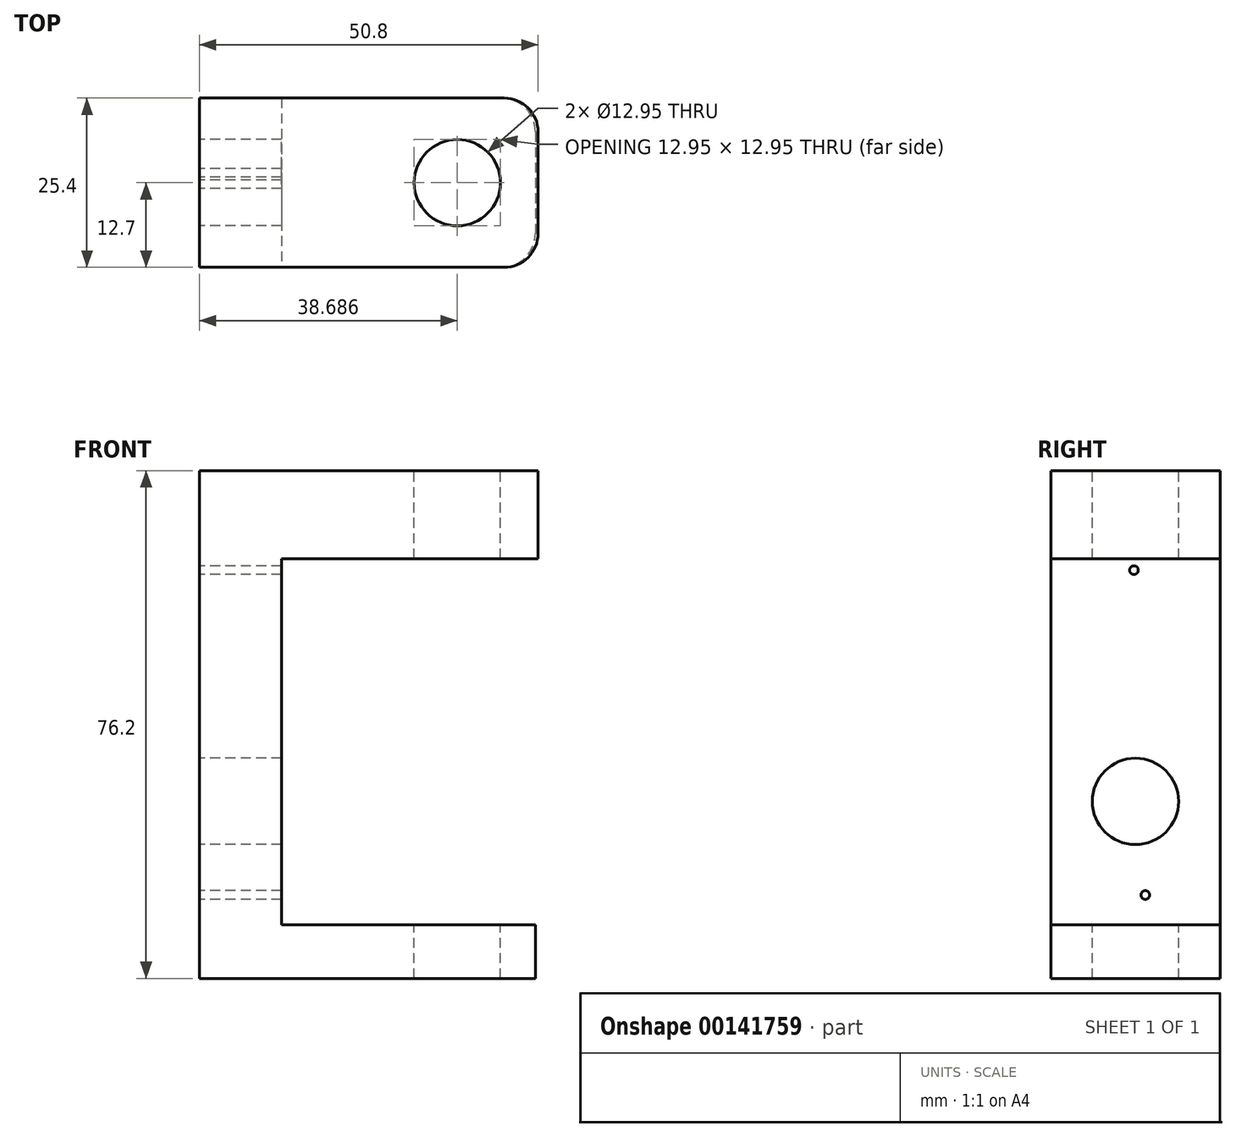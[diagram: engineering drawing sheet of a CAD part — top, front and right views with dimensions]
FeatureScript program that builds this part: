
annotation { "Feature Type Name" : "Feature", "Feature Type Description" : "" }
export const myFeature = defineFeature(function(context is Context, id is Id, definition is map)
    precondition{}
    {
        {
            var Q0;
            Q0=qCreatedBy(makeId("Top.planeOp"),FACE);
            var sketch = newSketch(context, id + "F0", { "sketchPlane" : qUnion([Q0])});
            skLineSegment(sketch, "E0.bottom", {"start": v(0, 0) * mm, "end": v(-50.8, 0) * mm});
            skLineSegment(sketch, "E0.top", {"start": v(0, 25.4) * mm, "end": v(-50.8, 25.4) * mm});
            skLineSegment(sketch, "E0.left", {"start": v(0, 0) * mm, "end": v(0, 25.4) * mm});
            skLineSegment(sketch, "E0.right", {"start": v(-50.8, 0) * mm, "end": v(-50.8, 25.4) * mm});
            skSolve(sketch);
        }
        {
            var Q0;
            Q0=makeQuery(id+"F0.imprint","IMPRINT",FACE,{"disambiguationData":[TD([[makeQuery(id+"F0.imprint","IMPRINT",EDGE,{"derivedFrom":sQuery(id+"F0.wireOp",EDGE,"E0.bottom")}),-1.0]])]});
            extrude(context, id + "F1", {"entities" : qUnion([Q0]), "depth" : 76.2 * mm});
        }
        {
            var Q0;
            Q0=makeQuery(id+"F1.opExtrude","SWEPT_FACE",FACE,{"disambiguationData":[OSD([sQuery(id+"F0.wireOp",EDGE,"E0.bottom")])]});
            var sketch = newSketch(context, id + "F2", { "sketchPlane" : qUnion([Q0])});
            skLineSegment(sketch, "E1.bottom", {"start": v(-38.5, 0) * mm, "end": v(0, 0) * mm});
            skLineSegment(sketch, "E1.top", {"start": v(-38.5, 63) * mm, "end": v(0, 63) * mm});
            skLineSegment(sketch, "E1.left", {"start": v(-38.5, 0) * mm, "end": v(-38.5, 63) * mm});
            skLineSegment(sketch, "E1.right", {"start": v(0, 0) * mm, "end": v(0, 63) * mm});
            skSolve(sketch);
        }
        {
            var Q0;
            Q0=makeQuery(id+"F2.imprint","IMPRINT",FACE,{"disambiguationData":[TD([[makeQuery(id+"F2.imprint","IMPRINT",EDGE,{"derivedFrom":sQuery(id+"F2.wireOp",EDGE,"E1.bottom")}),-1.0]])]});
            extrude(context, id + "F3", {"entities" : qUnion([Q0]), "operationType" : NewBodyOperationType.REMOVE, "oppositeDirection" : true, "depth" : 50.8 * mm});
        }
        {
            var Q0;
            Q0=makeQuery(id+"F1.opExtrude","CAP_FACE",FACE,{"disambiguationData":[OSD([sQuery(id+"F0.wireOp",EDGE,"E0.bottom"),sQuery(id+"F0.wireOp",EDGE,"E0.top"),sQuery(id+"F0.wireOp",EDGE,"E0.left"),sQuery(id+"F0.wireOp",EDGE,"E0.right")])],"isStart":false});
            var sketch = newSketch(context, id + "F4", { "sketchPlane" : qUnion([Q0])});
            skCircle(sketch, "E2", {"center": v(-12.11, 12.7) * mm, "radius": 6.48 * mm});
            skPoint(sketch, "E2.centerSnap0", {"position": v(-50.8, 12.7) * mm});
            skSolve(sketch);
        }
        {
            var Q0;
            Q0=makeQuery(id+"F1.opExtrude","SWEPT_FACE",FACE,{"disambiguationData":[OSD([sQuery(id+"F0.wireOp",EDGE,"E0.right")])]});
            var sketch = newSketch(context, id + "F5", { "sketchPlane" : qUnion([Q0])});
            skCircle(sketch, "E3", {"center": v(-12.7, 26.55) * mm, "radius": 6.48 * mm});
            skPoint(sketch, "E3.centerSnap0", {"position": v(-12.7, 76.2) * mm});
            skSolve(sketch);
        }
        {
            var Q0;
            Q0=makeQuery(id+"F5.imprint","IMPRINT",FACE,{"disambiguationData":[TD([[makeQuery(id+"F5.imprint","IMPRINT",EDGE,{"derivedFrom":sQuery(id+"F5.wireOp",EDGE,"E3")}),1.0]])]});
            extrude(context, id + "F6", {"entities" : qUnion([Q0]), "operationType" : NewBodyOperationType.REMOVE, "oppositeDirection" : true, "depth" : 25.4 * mm});
        }
        {
            var Q0;
            Q0=makeQuery(id+"F3.boolean.opBoolean","COPY",FACE,{"derivedFrom":makeQuery(id+"F3.opExtrude","SWEPT_FACE",FACE,{"disambiguationData":[OSD([sQuery(id+"F2.wireOp",EDGE,"E1.left")])]})});
            var sketch = newSketch(context, id + "F7", { "sketchPlane" : qUnion([Q0])});
            skLineSegment(sketch, "E4.bottom", {"start": v(25.4, 8.05) * mm, "end": v(0, 8.05) * mm});
            skLineSegment(sketch, "E4.top", {"start": v(25.4, 0) * mm, "end": v(0, 0) * mm});
            skLineSegment(sketch, "E4.left", {"start": v(25.4, 8.05) * mm, "end": v(25.4, 0) * mm});
            skLineSegment(sketch, "E4.right", {"start": v(0, 8.05) * mm, "end": v(0, 0) * mm});
            skSolve(sketch);
        }
        {
            var Q0;
            Q0=makeQuery(id+"F7.imprint","IMPRINT",FACE,{"disambiguationData":[TD([[makeQuery(id+"F7.imprint","IMPRINT",EDGE,{"derivedFrom":sQuery(id+"F7.wireOp",EDGE,"E4.bottom")}),1.0]])]});
            extrude(context, id + "F8", {"entities" : qUnion([Q0]), "operationType" : NewBodyOperationType.ADD, "depth" : 38.1 * mm});
        }
        {
            var Q0;
            Q0=makeQuery(id+"F4.imprint","IMPRINT",FACE,{"disambiguationData":[TD([[makeQuery(id+"F4.imprint","IMPRINT",EDGE,{"derivedFrom":sQuery(id+"F4.wireOp",EDGE,"E2")}),1.0]])]});
            extrude(context, id + "F9", {"entities" : qUnion([Q0]), "operationType" : NewBodyOperationType.REMOVE, "oppositeDirection" : true, "depth" : 101.6 * mm});
        }
        {
            var Q0;
            Q0=makeQuery(id+"F1.opExtrude","SWEPT_EDGE",EDGE,{"disambiguationData":[OSD([sQuery(id+"F0.wireOp",EDGE,"E0.bottom"),sQuery(id+"F0.wireOp",EDGE,"E0.left")])]});
            var Q1;
            Q1=makeQuery(id+"F8.opExtrude","CAP_EDGE",EDGE,{"disambiguationData":[OSD([sQuery(id+"F7.wireOp",EDGE,"E4.right")])],"isStart":false});
            var Q2;
            Q2=makeQuery(id+"F8.opExtrude","CAP_EDGE",EDGE,{"disambiguationData":[OSD([sQuery(id+"F7.wireOp",EDGE,"E4.left")])],"isStart":false});
            var Q3;
            Q3=makeQuery(id+"F1.opExtrude","SWEPT_EDGE",EDGE,{"disambiguationData":[OSD([sQuery(id+"F0.wireOp",EDGE,"E0.top"),sQuery(id+"F0.wireOp",EDGE,"E0.left")])]});
            fillet(context, id + "F10", {"entities" : qUnion([Q0, Q1, Q2, Q3]), "radius" : 5.08 * mm, "tangentPropagation" : true, "allowEdgeOverflow" : false});
        }
        {
            var Q0;
            Q0=makeQuery(id+"F1.opExtrude","SWEPT_FACE",FACE,{"disambiguationData":[OSD([sQuery(id+"F0.wireOp",EDGE,"E0.right")])]});
            var sketch = newSketch(context, id + "F11", { "sketchPlane" : qUnion([Q0])});
            skCircle(sketch, "E5", {"center": v(-12.46, 61.27) * mm, "radius": 0.65 * mm});
            skCircle(sketch, "E6", {"center": v(-14.18, 12.52) * mm, "radius": 0.65 * mm});
            skSolve(sketch);
        }
        {
            var Q0;
            Q0 = qSketchRegion(id + "F11", true);
            extrude(context, id + "F12", {"entities" : qUnion([Q0]), "operationType" : NewBodyOperationType.REMOVE, "oppositeDirection" : true, "depth" : 25.4 * mm});
        }
    });
